# Revit family: Gira_540500
name_source: partatom
category: Electrical Fixtures
revit_build: Autodesk Revit 2017 (Build: 20160225_1515(x64)
units: mm (PartAtom-declared; Revit-internal decimal feet)

## family parameters
Cut with Voids When Loaded = No
Host = Face
Maintain Annotation Orientation = Yes
Part Type = Normal
Room Calculation Point = No
Round Connector Dimension = Use Diameter
Shared = No

## types (1)
- S3000 elektr. Schalteins. Einsatz
    Ausführung = sonstige
    Ausführung der Oberfläche = nicht zutreffend
    Available = Yes
    Befestigungsart = Krallen-/Schraubbefestigung
    Category = Elektronischer Schalter
    Data sheet (1) = https://katalog.gira.de
    Default Elevation = 1219 mm
    Farbe = sonstige
    GTIN = 4010337048299
    HAN = 540500
    HeinzeBIM = https://bimportal.heinze.de
    Keynote = Einsatz_1fach
    Lastart = sonstige
    Lichtwertspeicher = No
    Manufacturer URL = https://www.gira.de
    Montageart = unter Putz
    Name = S3000 elektr. Schalteins. Einsatz
    Oberfläche = sonstige
    Region = DE
    Transparent = No
    URL = http://katalog.gira.de
    Verwendbar mit IR-Taste = No
    Verwendbar mit Taste = Yes
    Verwendbar mit Zeitschalter/Timer = No
    Werkstoff = sonstige
    Werkstoffgüte = sonstige
    Zusammenstellung = Basiselement

## geometry (parser evidence)
native form markers: Blend x2, Sweep x3
no freeform markers — native parametric forms only
